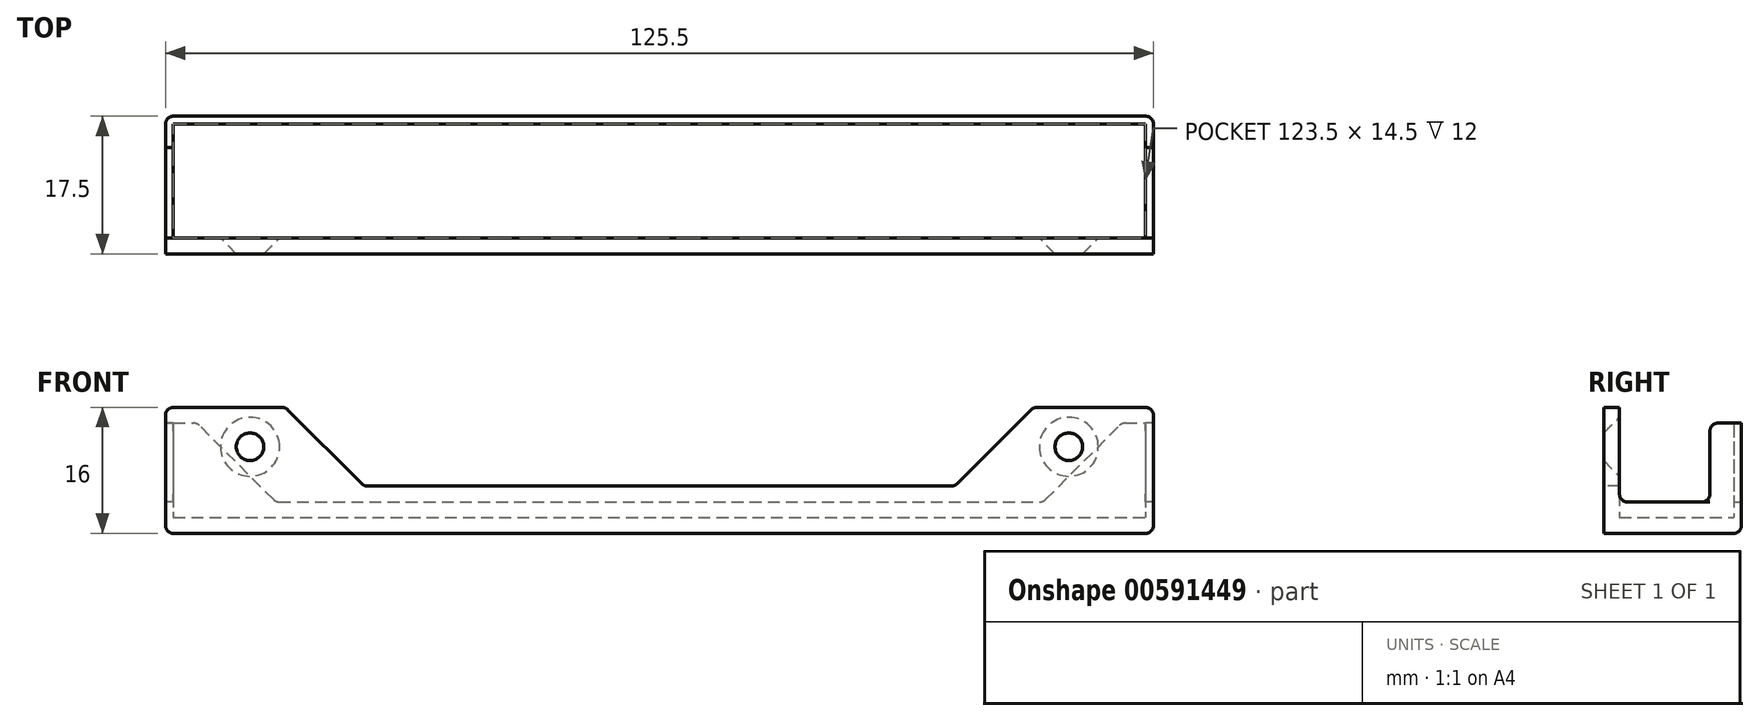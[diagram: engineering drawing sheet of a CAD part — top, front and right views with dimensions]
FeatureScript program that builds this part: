
annotation { "Feature Type Name" : "Feature", "Feature Type Description" : "" }
export const myFeature = defineFeature(function(context is Context, id is Id, definition is map)
    precondition{}
    {
        {
            var Q0;
            Q0=qCreatedBy(makeId("Top.planeOp"),FACE);
            var sketch = newSketch(context, id + "F0", { "sketchPlane" : qUnion([Q0])});
            skLineSegment(sketch, "E0.bottom", {"start": v(-62.75, 10.6) * mm, "end": v(62.75, 10.6) * mm});
            skLineSegment(sketch, "E0.top", {"start": v(-62.75, -6.9) * mm, "end": v(62.75, -6.9) * mm});
            skLineSegment(sketch, "E0.left", {"start": v(-62.75, 10.6) * mm, "end": v(-62.75, -6.9) * mm});
            skLineSegment(sketch, "E0.right", {"start": v(62.75, 10.6) * mm, "end": v(62.75, -6.9) * mm});
            skPoint(sketch, "E0.middle", {"position": v(0, 1.85) * mm});
            skSolve(sketch);
        }
        {
            var Q0;
            Q0 = qSketchRegion(id + "F0", true);
            extrude(context, id + "F1", {"entities" : qUnion([Q0]), "depth" : 2 * mm, "offsetDistance" : 25 * mm});
        }
        {
            var Q0;
            Q0=makeQuery(id+"F1.opExtrude","CAP_FACE",FACE,{"disambiguationData":[OSD([sQuery(id+"F0.wireOp",EDGE,"E0.bottom"),sQuery(id+"F0.wireOp",EDGE,"E0.top"),sQuery(id+"F0.wireOp",EDGE,"E0.left"),sQuery(id+"F0.wireOp",EDGE,"E0.right")])],"isStart":false});
            var sketch = newSketch(context, id + "F2", { "sketchPlane" : qUnion([Q0])});
            skLineSegment(sketch, "E1.bottom", {"start": v(-62.75, 10.6) * mm, "end": v(62.75, 10.6) * mm});
            skLineSegment(sketch, "E1.top", {"start": v(-62.75, 9.6) * mm, "end": v(62.75, 9.6) * mm});
            skLineSegment(sketch, "E1.left", {"start": v(-62.75, 10.6) * mm, "end": v(-62.75, 9.6) * mm});
            skLineSegment(sketch, "E1.right", {"start": v(62.75, 10.6) * mm, "end": v(62.75, 9.6) * mm});
            skLineSegment(sketch, "E2.bottom", {"start": v(62.75, -6.9) * mm, "end": v(61.75, -6.9) * mm});
            skLineSegment(sketch, "E2.top", {"start": v(62.75, 9.6) * mm, "end": v(61.75, 9.6) * mm});
            skLineSegment(sketch, "E2.left", {"start": v(62.75, -6.9) * mm, "end": v(62.75, 9.6) * mm});
            skLineSegment(sketch, "E2.right", {"start": v(61.75, -6.9) * mm, "end": v(61.75, 9.6) * mm});
            skLineSegment(sketch, "E3.bottom", {"start": v(-62.75, -6.9) * mm, "end": v(-61.75, -6.9) * mm});
            skLineSegment(sketch, "E3.top", {"start": v(-62.75, 9.6) * mm, "end": v(-61.75, 9.6) * mm});
            skLineSegment(sketch, "E3.left", {"start": v(-62.75, -6.9) * mm, "end": v(-62.75, 9.6) * mm});
            skLineSegment(sketch, "E3.right", {"start": v(-61.75, -6.9) * mm, "end": v(-61.75, 9.6) * mm});
            skSolve(sketch);
        }
        {
            var Q0;
            Q0 = qSketchRegion(id + "F2", true);
            extrude(context, id + "F3", {"entities" : qUnion([Q0]), "operationType" : NewBodyOperationType.ADD, "depth" : 2 * mm, "offsetDistance" : 25 * mm});
        }
        {
            var Q0;
            Q0=makeQuery(id+"F1.opExtrude","CAP_FACE",FACE,{"disambiguationData":[OSD([sQuery(id+"F0.wireOp",EDGE,"E0.bottom"),sQuery(id+"F0.wireOp",EDGE,"E0.top"),sQuery(id+"F0.wireOp",EDGE,"E0.left"),sQuery(id+"F0.wireOp",EDGE,"E0.right")])],"isStart":false});
            var sketch = newSketch(context, id + "F4", { "sketchPlane" : qUnion([Q0])});
            skLineSegment(sketch, "E4.bottom", {"start": v(-62.75, -6.9) * mm, "end": v(62.75, -6.9) * mm});
            skLineSegment(sketch, "E4.top", {"start": v(-62.75, -4.9) * mm, "end": v(62.75, -4.9) * mm});
            skLineSegment(sketch, "E4.left", {"start": v(-62.75, -6.9) * mm, "end": v(-62.75, -4.9) * mm});
            skLineSegment(sketch, "E4.right", {"start": v(62.75, -6.9) * mm, "end": v(62.75, -4.9) * mm});
            skSolve(sketch);
        }
        {
            var Q0;
            Q0 = qSketchRegion(id + "F4", true);
            extrude(context, id + "F5", {"entities" : qUnion([Q0]), "operationType" : NewBodyOperationType.ADD, "depth" : 14 * mm, "offsetDistance" : 25 * mm});
        }
        {
            var Q0;
            Q0=makeQuery(id+"F5.opExtrude","SWEPT_FACE",FACE,{"disambiguationData":[OSD([sQuery(id+"F4.wireOp",EDGE,"E4.top")])]});
            var sketch = newSketch(context, id + "F6", { "sketchPlane" : qUnion([Q0])});
            skLineSegment(sketch, "E5", {"start": v(-52, 11) * mm, "end": v(52, 11) * mm});
            skSolve(sketch);
        }
        {
            var Q0;
            Q0=sQuery(id+"F6.wireOp",VERTEX,"E5.start");
            var Q1;
            Q1=sQuery(id+"F6.wireOp",VERTEX,"E5.end");
            var Q2;
            Q2=makeQuery(id+"F1.opExtrude","SWEPT_BODY",BODY,{"disambiguationData":[OSD([sQuery(id+"F0.wireOp",EDGE,"E0.bottom"),sQuery(id+"F0.wireOp",EDGE,"E0.top"),sQuery(id+"F0.wireOp",EDGE,"E0.left"),sQuery(id+"F0.wireOp",EDGE,"E0.right")])]});
            hole(context, id + "F7", {"style" : HoleStyle.C_SINK, "endStyle" : HoleEndStyle.THROUGH, "holeDiameter" : 3.2 * mm, "cSinkDiameter" : 7.5 * mm, "cSinkAngle" : 90 * degree, "majorDiameter" : 5 * mm, "isTappedThrough" : true, "tappedDepth" : 12 * mm, "tapClearance" : 3, "locations" : qUnion([Q0, Q1]), "scope" : qUnion([Q2])});
        }
        {
            var Q0;
            Q0=makeQuery(id+"F5.opExtrude","SWEPT_FACE",FACE,{"disambiguationData":[OSD([sQuery(id+"F4.wireOp",EDGE,"E4.top")])]});
            var sketch = newSketch(context, id + "F8", { "sketchPlane" : qUnion([Q0])});
            skLineSegment(sketch, "E6.bottom", {"start": v(-47.5, 16) * mm, "end": v(47.5, 16) * mm});
            skLineSegment(sketch, "E6.top", {"start": v(-47.5, 6) * mm, "end": v(47.5, 6) * mm});
            skLineSegment(sketch, "E6.left", {"start": v(-47.5, 16) * mm, "end": v(-47.5, 6) * mm});
            skLineSegment(sketch, "E6.right", {"start": v(47.5, 16) * mm, "end": v(47.5, 6) * mm});
            skSolve(sketch);
        }
        {
            var Q0;
            Q0 = qSketchRegion(id + "F8", true);
            extrude(context, id + "F9", {"entities" : qUnion([Q0]), "operationType" : NewBodyOperationType.REMOVE, "oppositeDirection" : true, "depth" : 25 * mm, "offsetDistance" : 25 * mm});
        }
        {
            var Q0;
            Q0=makeQuery(id+"F3.opExtrude","CAP_FACE",FACE,{"disambiguationData":[OSD([sQuery(id+"F2.wireOp",EDGE,"E1.bottom"),sQuery(id+"F2.wireOp",EDGE,"E1.top"),sQuery(id+"F2.wireOp",EDGE,"E1.left"),sQuery(id+"F2.wireOp",EDGE,"E1.right"),sQuery(id+"F2.wireOp",EDGE,"E2.bottom"),sQuery(id+"F2.wireOp",EDGE,"E2.left"),sQuery(id+"F2.wireOp",EDGE,"E2.right"),sQuery(id+"F2.wireOp",EDGE,"E3.bottom"),sQuery(id+"F2.wireOp",EDGE,"E3.left"),sQuery(id+"F2.wireOp",EDGE,"E3.right")])],"isStart":false});
            var sketch = newSketch(context, id + "F10", { "sketchPlane" : qUnion([Q0])});
            skLineSegment(sketch, "E7.bottom", {"start": v(62.75, 10.6) * mm, "end": v(58.75, 10.6) * mm});
            skLineSegment(sketch, "E7.top", {"start": v(61.75, 9.6) * mm, "end": v(58.75, 9.6) * mm});
            skLineSegment(sketch, "E7.left", {"start": v(62.75, 10.6) * mm, "end": v(62.75, 9.6) * mm});
            skLineSegment(sketch, "E7.right", {"start": v(58.75, 10.6) * mm, "end": v(58.75, 9.6) * mm});
            skLineSegment(sketch, "E8.top", {"start": v(62.75, 6.6) * mm, "end": v(61.75, 6.6) * mm});
            skLineSegment(sketch, "E8.left", {"start": v(62.75, 9.6) * mm, "end": v(62.75, 6.6) * mm});
            skLineSegment(sketch, "E8.right", {"start": v(61.75, 9.6) * mm, "end": v(61.75, 6.6) * mm});
            skLineSegment(sketch, "E9.MirrorCS", {"start": v(-62.75, 9.6) * mm, "end": v(-62.75, 6.6) * mm});
            skLineSegment(sketch, "E10.MirrorCS", {"start": v(-62.75, 10.6) * mm, "end": v(-62.75, 9.6) * mm});
            skLineSegment(sketch, "E11.MirrorCS", {"start": v(-62.75, 10.6) * mm, "end": v(-58.75, 10.6) * mm});
            skLineSegment(sketch, "E12.MirrorCS", {"start": v(-58.75, 10.6) * mm, "end": v(-58.75, 9.6) * mm});
            skLineSegment(sketch, "E13.MirrorCS", {"start": v(-61.75, 9.6) * mm, "end": v(-58.75, 9.6) * mm});
            skLineSegment(sketch, "E14.MirrorCS", {"start": v(-61.75, 9.6) * mm, "end": v(-61.75, 6.6) * mm});
            skLineSegment(sketch, "E15.MirrorCS", {"start": v(-62.75, 6.6) * mm, "end": v(-61.75, 6.6) * mm});
            skSolve(sketch);
        }
        {
            var Q0;
            Q0 = qSketchRegion(id + "F10", true);
            extrude(context, id + "F11", {"entities" : qUnion([Q0]), "operationType" : NewBodyOperationType.ADD, "depth" : 10 * mm, "offsetDistance" : 25 * mm});
        }
        {
            var Q0;
            Q0=makeQuery(id+"F11.opExtrude","CAP_EDGE",EDGE,{"disambiguationData":[OSD([sQuery(id+"F10.wireOp",EDGE,"E7.right")])],"isStart":true});
            var Q1;
            Q1=makeQuery(id+"F11.opExtrude","CAP_EDGE",EDGE,{"disambiguationData":[OSD([sQuery(id+"F10.wireOp",EDGE,"E12.MirrorCS")])],"isStart":true});
            var Q2;
            Q2=makeQuery(id+"F9.boolean.opBoolean","COPY",EDGE,{"derivedFrom":makeQuery(id+"F9.opExtrude","SWEPT_EDGE",EDGE,{"disambiguationData":[OSD([sQuery(id+"F8.wireOp",EDGE,"E6.top"),sQuery(id+"F8.wireOp",EDGE,"E6.left")])]})});
            var Q3;
            Q3=makeQuery(id+"F9.boolean.opBoolean","COPY",EDGE,{"derivedFrom":makeQuery(id+"F9.opExtrude","SWEPT_EDGE",EDGE,{"disambiguationData":[OSD([sQuery(id+"F8.wireOp",EDGE,"E6.top"),sQuery(id+"F8.wireOp",EDGE,"E6.right")])]})});
            chamfer(context, id + "F12", {"entities" : qUnion([Q0, Q1, Q2, Q3]), "width" : 10 * mm, "tangentPropagation" : true});
        }
        {
            var Q0;
            Q0=makeQuery(id+"F5.boolean.opBoolean","INTERSECT",EDGE,{"disambiguationData":[OD(1.0)],"derivedFrom":[makeQuery(id+"F3.opExtrude","CAP_FACE",FACE,{"disambiguationData":[OSD([sQuery(id+"F2.wireOp",EDGE,"E1.bottom"),sQuery(id+"F2.wireOp",EDGE,"E1.top"),sQuery(id+"F2.wireOp",EDGE,"E1.left"),sQuery(id+"F2.wireOp",EDGE,"E1.right"),sQuery(id+"F2.wireOp",EDGE,"E2.bottom"),sQuery(id+"F2.wireOp",EDGE,"E2.left"),sQuery(id+"F2.wireOp",EDGE,"E2.right"),sQuery(id+"F2.wireOp",EDGE,"E3.bottom"),sQuery(id+"F2.wireOp",EDGE,"E3.left"),sQuery(id+"F2.wireOp",EDGE,"E3.right")])],"isStart":false}),makeQuery(id+"F5.opExtrude","SWEPT_FACE",FACE,{"disambiguationData":[OSD([sQuery(id+"F4.wireOp",EDGE,"E4.top")])]})]});
            var Q1;
            Q1=makeQuery(id+"F11.opExtrude","CAP_EDGE",EDGE,{"disambiguationData":[OSD([sQuery(id+"F10.wireOp",EDGE,"E8.top")])],"isStart":true});
            var Q2;
            Q2=makeQuery(id+"F11.opExtrude","CAP_EDGE",EDGE,{"disambiguationData":[OSD([sQuery(id+"F10.wireOp",EDGE,"E8.top")])],"isStart":false});
            var Q3;
            {var subQ0=sQuery(id+"F10.wireOp",EDGE,"E7.right");Q3=makeQuery(id+"F12.opChamfer","BLEND_EDGE",EDGE,{"blendedFrom":[makeQuery(id+"F11.opExtrude","CAP_EDGE",EDGE,{"disambiguationData":[OSD([subQ0])],"isStart":true}),makeQuery(id+"F11.opExtrude","CAP_FACE",FACE,{"disambiguationData":[OSD([sQuery(id+"F10.wireOp",EDGE,"E7.bottom"),sQuery(id+"F10.wireOp",EDGE,"E7.top"),sQuery(id+"F10.wireOp",EDGE,"E7.left"),subQ0,sQuery(id+"F10.wireOp",EDGE,"E8.top"),sQuery(id+"F10.wireOp",EDGE,"E8.left"),sQuery(id+"F10.wireOp",EDGE,"E8.right")])],"isStart":false})],"blendedInto":[makeQuery(id+"F11.opExtrude","CAP_FACE",FACE,{"disambiguationData":[OSD([sQuery(id+"F10.wireOp",EDGE,"E7.bottom"),sQuery(id+"F10.wireOp",EDGE,"E7.top"),sQuery(id+"F10.wireOp",EDGE,"E7.left"),subQ0,sQuery(id+"F10.wireOp",EDGE,"E8.top"),sQuery(id+"F10.wireOp",EDGE,"E8.left"),sQuery(id+"F10.wireOp",EDGE,"E8.right")])],"isStart":false})]});}
            var Q4;
            {var subQ0=sQuery(id+"F2.wireOp",EDGE,"E1.top");var subQ1=sQuery(id+"F2.wireOp",EDGE,"E1.bottom");var subQ2=sQuery(id+"F10.wireOp",EDGE,"E7.right");Q4=makeQuery(id+"F12.opChamfer","BLEND_EDGE",EDGE,{"blendedFrom":[makeQuery(id+"F11.opExtrude","CAP_EDGE",EDGE,{"disambiguationData":[OSD([subQ2])],"isStart":true}),makeQuery(id+"F11.boolean.opBoolean","SPLIT",FACE,{"disambiguationData":[TD([makeQuery(id+"F1.opExtrude","SWEPT_FACE",FACE,{"disambiguationData":[OSD([sQuery(id+"F0.wireOp",EDGE,"E0.bottom")])]})])],"derivedFrom":makeQuery(id+"F3.opExtrude","CAP_FACE",FACE,{"disambiguationData":[OSD([subQ1,subQ0,sQuery(id+"F2.wireOp",EDGE,"E1.left"),sQuery(id+"F2.wireOp",EDGE,"E1.right"),sQuery(id+"F2.wireOp",EDGE,"E2.bottom"),sQuery(id+"F2.wireOp",EDGE,"E2.left"),sQuery(id+"F2.wireOp",EDGE,"E2.right"),sQuery(id+"F2.wireOp",EDGE,"E3.bottom"),sQuery(id+"F2.wireOp",EDGE,"E3.left"),sQuery(id+"F2.wireOp",EDGE,"E3.right")])],"isStart":false})})],"blendedInto":[makeQuery(id+"F11.boolean.opBoolean","SPLIT",FACE,{"disambiguationData":[TD([makeQuery(id+"F1.opExtrude","SWEPT_FACE",FACE,{"disambiguationData":[OSD([sQuery(id+"F0.wireOp",EDGE,"E0.bottom")])]})])],"derivedFrom":makeQuery(id+"F3.opExtrude","CAP_FACE",FACE,{"disambiguationData":[OSD([subQ1,subQ0,sQuery(id+"F2.wireOp",EDGE,"E1.left"),sQuery(id+"F2.wireOp",EDGE,"E1.right"),sQuery(id+"F2.wireOp",EDGE,"E2.bottom"),sQuery(id+"F2.wireOp",EDGE,"E2.left"),sQuery(id+"F2.wireOp",EDGE,"E2.right"),sQuery(id+"F2.wireOp",EDGE,"E3.bottom"),sQuery(id+"F2.wireOp",EDGE,"E3.left"),sQuery(id+"F2.wireOp",EDGE,"E3.right")])],"isStart":false})})]});}
            var Q5;
            Q5=makeQuery(id+"F11.boolean.opBoolean","MERGE",EDGE,{"derivedFrom":[makeQuery(id+"F3.boolean.opBoolean","MERGE",EDGE,{"derivedFrom":[makeQuery(id+"F1.opExtrude","SWEPT_EDGE",EDGE,{"disambiguationData":[OSD([sQuery(id+"F0.wireOp",EDGE,"E0.bottom"),sQuery(id+"F0.wireOp",EDGE,"E0.right")])]}),makeQuery(id+"F3.opExtrude","SWEPT_EDGE",EDGE,{"disambiguationData":[OSD([sQuery(id+"F2.wireOp",EDGE,"E1.bottom"),sQuery(id+"F2.wireOp",EDGE,"E1.right")])]})]}),makeQuery(id+"F11.opExtrude","SWEPT_EDGE",EDGE,{"disambiguationData":[OSD([sQuery(id+"F10.wireOp",EDGE,"E7.bottom"),sQuery(id+"F10.wireOp",EDGE,"E7.left")])]})]});
            var Q6;
            {var subQ0=sQuery(id+"F2.wireOp",EDGE,"E1.top");var subQ1=sQuery(id+"F2.wireOp",EDGE,"E1.bottom");var subQ2=sQuery(id+"F10.wireOp",EDGE,"E12.MirrorCS");Q6=makeQuery(id+"F12.opChamfer","BLEND_EDGE",EDGE,{"blendedFrom":[makeQuery(id+"F11.opExtrude","CAP_EDGE",EDGE,{"disambiguationData":[OSD([subQ2])],"isStart":true}),makeQuery(id+"F11.boolean.opBoolean","SPLIT",FACE,{"disambiguationData":[TD([makeQuery(id+"F1.opExtrude","SWEPT_FACE",FACE,{"disambiguationData":[OSD([sQuery(id+"F0.wireOp",EDGE,"E0.bottom")])]})])],"derivedFrom":makeQuery(id+"F3.opExtrude","CAP_FACE",FACE,{"disambiguationData":[OSD([subQ1,subQ0,sQuery(id+"F2.wireOp",EDGE,"E1.left"),sQuery(id+"F2.wireOp",EDGE,"E1.right"),sQuery(id+"F2.wireOp",EDGE,"E2.bottom"),sQuery(id+"F2.wireOp",EDGE,"E2.left"),sQuery(id+"F2.wireOp",EDGE,"E2.right"),sQuery(id+"F2.wireOp",EDGE,"E3.bottom"),sQuery(id+"F2.wireOp",EDGE,"E3.left"),sQuery(id+"F2.wireOp",EDGE,"E3.right")])],"isStart":false})})],"blendedInto":[makeQuery(id+"F11.boolean.opBoolean","SPLIT",FACE,{"disambiguationData":[TD([makeQuery(id+"F1.opExtrude","SWEPT_FACE",FACE,{"disambiguationData":[OSD([sQuery(id+"F0.wireOp",EDGE,"E0.bottom")])]})])],"derivedFrom":makeQuery(id+"F3.opExtrude","CAP_FACE",FACE,{"disambiguationData":[OSD([subQ1,subQ0,sQuery(id+"F2.wireOp",EDGE,"E1.left"),sQuery(id+"F2.wireOp",EDGE,"E1.right"),sQuery(id+"F2.wireOp",EDGE,"E2.bottom"),sQuery(id+"F2.wireOp",EDGE,"E2.left"),sQuery(id+"F2.wireOp",EDGE,"E2.right"),sQuery(id+"F2.wireOp",EDGE,"E3.bottom"),sQuery(id+"F2.wireOp",EDGE,"E3.left"),sQuery(id+"F2.wireOp",EDGE,"E3.right")])],"isStart":false})})]});}
            var Q7;
            {var subQ0=sQuery(id+"F10.wireOp",EDGE,"E12.MirrorCS");Q7=makeQuery(id+"F12.opChamfer","BLEND_EDGE",EDGE,{"blendedFrom":[makeQuery(id+"F11.opExtrude","CAP_EDGE",EDGE,{"disambiguationData":[OSD([subQ0])],"isStart":true}),makeQuery(id+"F11.opExtrude","CAP_FACE",FACE,{"disambiguationData":[OSD([sQuery(id+"F10.wireOp",EDGE,"E10.MirrorCS"),sQuery(id+"F10.wireOp",EDGE,"E11.MirrorCS"),subQ0,sQuery(id+"F10.wireOp",EDGE,"E13.MirrorCS"),sQuery(id+"F10.wireOp",EDGE,"E14.MirrorCS"),sQuery(id+"F10.wireOp",EDGE,"E15.MirrorCS"),sQuery(id+"F10.wireOp",EDGE,"E9.MirrorCS")])],"isStart":false})],"blendedInto":[makeQuery(id+"F11.opExtrude","CAP_FACE",FACE,{"disambiguationData":[OSD([sQuery(id+"F10.wireOp",EDGE,"E10.MirrorCS"),sQuery(id+"F10.wireOp",EDGE,"E11.MirrorCS"),subQ0,sQuery(id+"F10.wireOp",EDGE,"E13.MirrorCS"),sQuery(id+"F10.wireOp",EDGE,"E14.MirrorCS"),sQuery(id+"F10.wireOp",EDGE,"E15.MirrorCS"),sQuery(id+"F10.wireOp",EDGE,"E9.MirrorCS")])],"isStart":false})]});}
            var Q8;
            Q8=makeQuery(id+"F11.boolean.opBoolean","MERGE",EDGE,{"derivedFrom":[makeQuery(id+"F3.boolean.opBoolean","MERGE",EDGE,{"derivedFrom":[makeQuery(id+"F1.opExtrude","SWEPT_EDGE",EDGE,{"disambiguationData":[OSD([sQuery(id+"F0.wireOp",EDGE,"E0.bottom"),sQuery(id+"F0.wireOp",EDGE,"E0.left")])]}),makeQuery(id+"F3.opExtrude","SWEPT_EDGE",EDGE,{"disambiguationData":[OSD([sQuery(id+"F2.wireOp",EDGE,"E1.bottom"),sQuery(id+"F2.wireOp",EDGE,"E1.left")])]})]}),makeQuery(id+"F11.opExtrude","SWEPT_EDGE",EDGE,{"disambiguationData":[OSD([sQuery(id+"F10.wireOp",EDGE,"E10.MirrorCS"),sQuery(id+"F10.wireOp",EDGE,"E11.MirrorCS")])]})]});
            var Q9;
            Q9=makeQuery(id+"F11.opExtrude","CAP_EDGE",EDGE,{"disambiguationData":[OSD([sQuery(id+"F10.wireOp",EDGE,"E15.MirrorCS")])],"isStart":false});
            var Q10;
            Q10=makeQuery(id+"F11.opExtrude","CAP_EDGE",EDGE,{"disambiguationData":[OSD([sQuery(id+"F10.wireOp",EDGE,"E15.MirrorCS")])],"isStart":true});
            var Q11;
            Q11=makeQuery(id+"F5.boolean.opBoolean","INTERSECT",EDGE,{"disambiguationData":[OD(0.0)],"derivedFrom":[makeQuery(id+"F3.opExtrude","CAP_FACE",FACE,{"disambiguationData":[OSD([sQuery(id+"F2.wireOp",EDGE,"E1.bottom"),sQuery(id+"F2.wireOp",EDGE,"E1.top"),sQuery(id+"F2.wireOp",EDGE,"E1.left"),sQuery(id+"F2.wireOp",EDGE,"E1.right"),sQuery(id+"F2.wireOp",EDGE,"E2.bottom"),sQuery(id+"F2.wireOp",EDGE,"E2.left"),sQuery(id+"F2.wireOp",EDGE,"E2.right"),sQuery(id+"F2.wireOp",EDGE,"E3.bottom"),sQuery(id+"F2.wireOp",EDGE,"E3.left"),sQuery(id+"F2.wireOp",EDGE,"E3.right")])],"isStart":false}),makeQuery(id+"F5.opExtrude","SWEPT_FACE",FACE,{"disambiguationData":[OSD([sQuery(id+"F4.wireOp",EDGE,"E4.top")])]})]});
            var Q12;
            Q12=makeQuery(id+"F1.opExtrude","CAP_EDGE",EDGE,{"disambiguationData":[OSD([sQuery(id+"F0.wireOp",EDGE,"E0.bottom")])],"isStart":true});
            var Q13;
            Q13=makeQuery(id+"F1.opExtrude","CAP_EDGE",EDGE,{"disambiguationData":[OSD([sQuery(id+"F0.wireOp",EDGE,"E0.left")])],"isStart":true});
            var Q14;
            Q14=makeQuery(id+"F1.opExtrude","CAP_EDGE",EDGE,{"disambiguationData":[OSD([sQuery(id+"F0.wireOp",EDGE,"E0.right")])],"isStart":true});
            var Q15;
            {var subQ0=sQuery(id+"F8.wireOp",EDGE,"E6.top");Q15=makeQuery(id+"F12.opChamfer","BLEND_EDGE",EDGE,{"blendedFrom":[makeQuery(id+"F9.boolean.opBoolean","COPY",EDGE,{"derivedFrom":makeQuery(id+"F9.opExtrude","SWEPT_EDGE",EDGE,{"disambiguationData":[OSD([subQ0,sQuery(id+"F8.wireOp",EDGE,"E6.left")])]})}),makeQuery(id+"F9.boolean.opBoolean","COPY",FACE,{"derivedFrom":makeQuery(id+"F9.opExtrude","SWEPT_FACE",FACE,{"disambiguationData":[OSD([subQ0])]})})],"blendedInto":[makeQuery(id+"F9.boolean.opBoolean","COPY",FACE,{"derivedFrom":makeQuery(id+"F9.opExtrude","SWEPT_FACE",FACE,{"disambiguationData":[OSD([subQ0])]})})]});}
            var Q16;
            {var subQ0=sQuery(id+"F4.wireOp",EDGE,"E4.bottom");var subQ1=sQuery(id+"F4.wireOp",EDGE,"E4.top");var subQ2=sQuery(id+"F4.wireOp",EDGE,"E4.right");var subQ3=sQuery(id+"F8.wireOp",EDGE,"E6.left");Q16=makeQuery(id+"F12.opChamfer","BLEND_EDGE",EDGE,{"blendedFrom":[makeQuery(id+"F9.boolean.opBoolean","COPY",EDGE,{"derivedFrom":makeQuery(id+"F9.opExtrude","SWEPT_EDGE",EDGE,{"disambiguationData":[OSD([sQuery(id+"F8.wireOp",EDGE,"E6.top"),subQ3])]})}),makeQuery(id+"F9.boolean.opBoolean","SPLIT",FACE,{"disambiguationData":[TD([makeQuery(id+"F1.opExtrude","SWEPT_FACE",FACE,{"disambiguationData":[OSD([sQuery(id+"F0.wireOp",EDGE,"E0.right")])]})])],"derivedFrom":makeQuery(id+"F5.opExtrude","CAP_FACE",FACE,{"disambiguationData":[OSD([subQ0,subQ1,sQuery(id+"F4.wireOp",EDGE,"E4.left"),subQ2])],"isStart":false})})],"blendedInto":[makeQuery(id+"F9.boolean.opBoolean","SPLIT",FACE,{"disambiguationData":[TD([makeQuery(id+"F1.opExtrude","SWEPT_FACE",FACE,{"disambiguationData":[OSD([sQuery(id+"F0.wireOp",EDGE,"E0.right")])]})])],"derivedFrom":makeQuery(id+"F5.opExtrude","CAP_FACE",FACE,{"disambiguationData":[OSD([subQ0,subQ1,sQuery(id+"F4.wireOp",EDGE,"E4.left"),subQ2])],"isStart":false})})]});}
            var Q17;
            Q17=makeQuery(id+"F5.opExtrude","CAP_EDGE",EDGE,{"disambiguationData":[OSD([sQuery(id+"F4.wireOp",EDGE,"E4.right")])],"isStart":false});
            var Q18;
            {var subQ0=sQuery(id+"F8.wireOp",EDGE,"E6.top");Q18=makeQuery(id+"F12.opChamfer","BLEND_EDGE",EDGE,{"blendedFrom":[makeQuery(id+"F9.boolean.opBoolean","COPY",EDGE,{"derivedFrom":makeQuery(id+"F9.opExtrude","SWEPT_EDGE",EDGE,{"disambiguationData":[OSD([subQ0,sQuery(id+"F8.wireOp",EDGE,"E6.right")])]})}),makeQuery(id+"F9.boolean.opBoolean","COPY",FACE,{"derivedFrom":makeQuery(id+"F9.opExtrude","SWEPT_FACE",FACE,{"disambiguationData":[OSD([subQ0])]})})],"blendedInto":[makeQuery(id+"F9.boolean.opBoolean","COPY",FACE,{"derivedFrom":makeQuery(id+"F9.opExtrude","SWEPT_FACE",FACE,{"disambiguationData":[OSD([subQ0])]})})]});}
            var Q19;
            {var subQ0=sQuery(id+"F4.wireOp",EDGE,"E4.top");var subQ1=sQuery(id+"F8.wireOp",EDGE,"E6.right");var subQ2=sQuery(id+"F4.wireOp",EDGE,"E4.bottom");var subQ3=sQuery(id+"F4.wireOp",EDGE,"E4.left");Q19=makeQuery(id+"F12.opChamfer","BLEND_EDGE",EDGE,{"blendedFrom":[makeQuery(id+"F9.boolean.opBoolean","COPY",EDGE,{"derivedFrom":makeQuery(id+"F9.opExtrude","SWEPT_EDGE",EDGE,{"disambiguationData":[OSD([sQuery(id+"F8.wireOp",EDGE,"E6.top"),subQ1])]})}),makeQuery(id+"F9.boolean.opBoolean","SPLIT",FACE,{"disambiguationData":[TD([makeQuery(id+"F1.opExtrude","SWEPT_FACE",FACE,{"disambiguationData":[OSD([sQuery(id+"F0.wireOp",EDGE,"E0.left")])]})])],"derivedFrom":makeQuery(id+"F5.opExtrude","CAP_FACE",FACE,{"disambiguationData":[OSD([subQ2,subQ0,subQ3,sQuery(id+"F4.wireOp",EDGE,"E4.right")])],"isStart":false})})],"blendedInto":[makeQuery(id+"F9.boolean.opBoolean","SPLIT",FACE,{"disambiguationData":[TD([makeQuery(id+"F1.opExtrude","SWEPT_FACE",FACE,{"disambiguationData":[OSD([sQuery(id+"F0.wireOp",EDGE,"E0.left")])]})])],"derivedFrom":makeQuery(id+"F5.opExtrude","CAP_FACE",FACE,{"disambiguationData":[OSD([subQ2,subQ0,subQ3,sQuery(id+"F4.wireOp",EDGE,"E4.right")])],"isStart":false})})]});}
            var Q20;
            Q20=makeQuery(id+"F5.opExtrude","CAP_EDGE",EDGE,{"disambiguationData":[OSD([sQuery(id+"F4.wireOp",EDGE,"E4.left")])],"isStart":false});
            fillet(context, id + "F13", {"entities" : qUnion([Q0, Q1, Q2, Q3, Q4, Q5, Q6, Q7, Q8, Q9, Q10, Q11, Q12, Q13, Q14, Q15, Q16, Q17, Q18, Q19, Q20]), "radius" : 1 * mm, "tangentPropagation" : true, "allowEdgeOverflow" : false});
        }
    });
